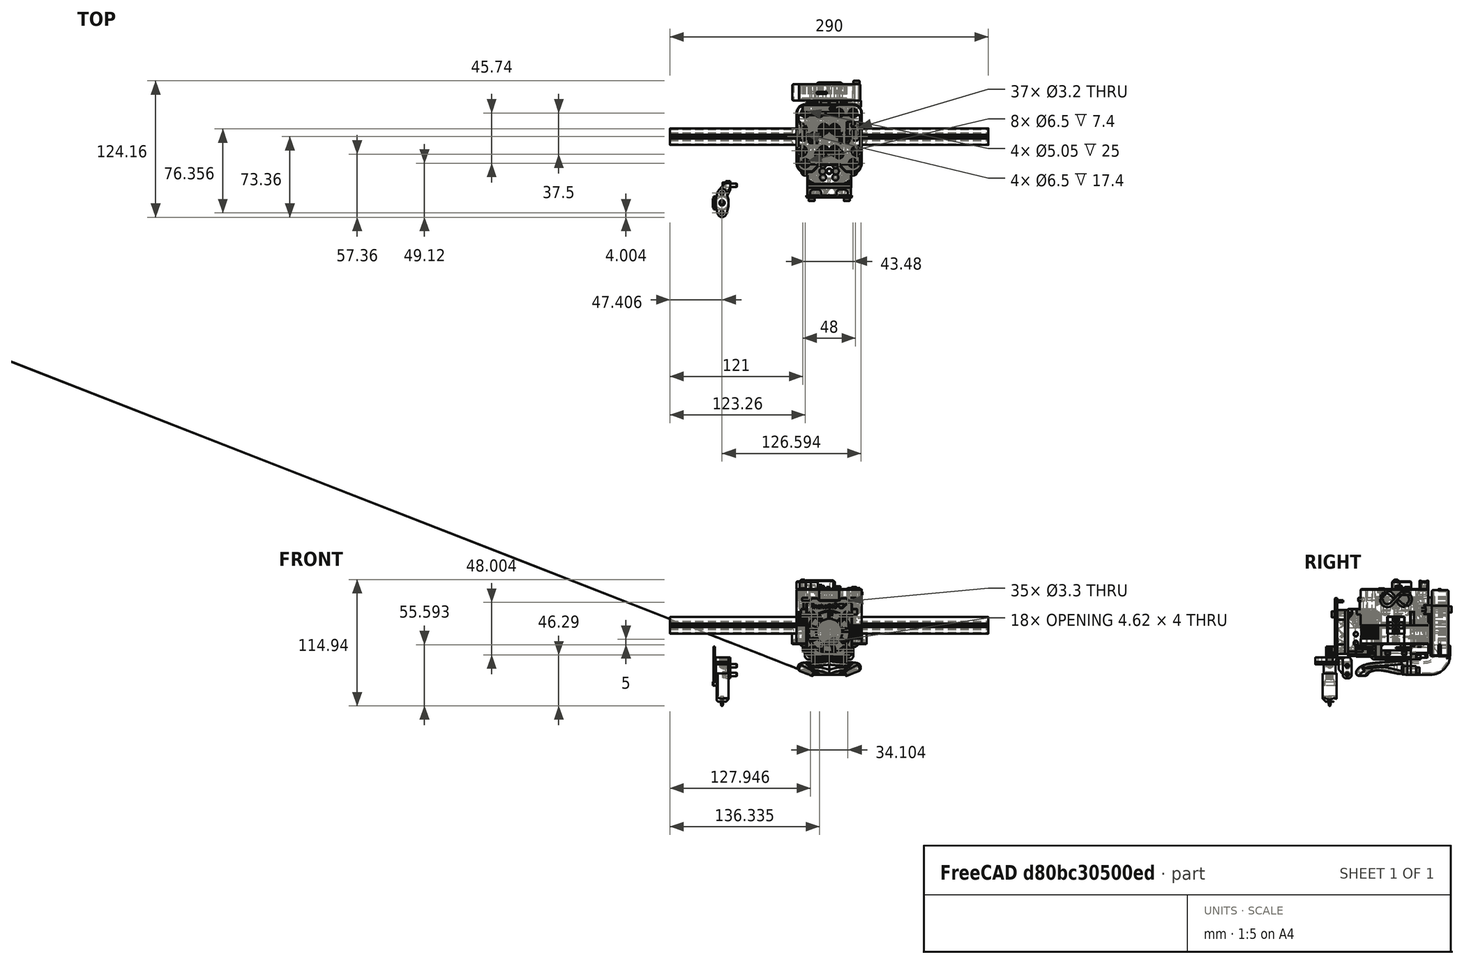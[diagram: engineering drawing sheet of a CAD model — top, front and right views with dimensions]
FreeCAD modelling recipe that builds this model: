
FCSTD DOCUMENT  (FreeCAD 0.19R24291 (Git))
Label: gantry-1515
License: Other
LicenseURL: GPL3
objects: Part::FeaturePython×95, Part::Feature×65, App::Part×6
note: 160 computed .brp shape members not serialized (recipe doc carries the construction recipe); baked Part::Feature solids carry a one-line shape summary decoded from their .brp

FEATURE [Part::FeaturePython] Screw003  label="M5x50-Screw"  # Fasteners workbench fastener (typed FeaturePython)
  Placement = pos=(9,-16,3) rot=(1,0,0;3.14159rad)
  diameter = 3
  invert = true
  length = 11
  lengthCustom = 50
  matchOuter = true
  offset = 0
  thread = false
  type = 39
FEATURE [Part::FeaturePython] Washer006  label="M3-Washer006"  # Fasteners workbench fastener (typed FeaturePython)
  Placement = pos=(-5,-13,50) rot=(0,0,1;0rad)
  diameter = 4
  invert = false
  matchOuter = true
  offset = 0
  type = 5
FEATURE [Part::FeaturePython] Screw009  label="M3x10-Screw004"  # Fasteners workbench fastener (typed FeaturePython)
  Placement = pos=(-5,-13,50.55) rot=(0,0,1;0rad)
  baseObject = -> Washer006 [Edge1]
  diameter = 4
  invert = false
  length = 3
  lengthCustom = 10
  matchOuter = true
  offset = 0
  thread = false
  type = 33
FEATURE [Part::FeaturePython] Screw005  label="M5x50-Screw005"  # Fasteners workbench fastener (typed FeaturePython)
  Placement = pos=(21.74,21.5,3) rot=(1,0,0;3.14159rad)
  diameter = 3
  invert = true
  length = 11
  lengthCustom = 50
  matchOuter = true
  offset = 0
  thread = false
  type = 39
FEATURE [Part::FeaturePython] Washer015  label="M3-Washer036"  # Fasteners workbench fastener (typed FeaturePython)
  Placement = pos=(24,0,35.55) rot=(0,0,1;0rad)
  diameter = 4
  invert = false
  matchOuter = true
  offset = 0
  type = 5
FEATURE [Part::FeaturePython] Washer011  label="M3-Washer039"  # Fasteners workbench fastener (typed FeaturePython)
  Placement = pos=(29,0,6.45) rot=(1,0,0;3.14159rad)
  diameter = 4
  invert = false
  matchOuter = true
  offset = 0
  type = 5
FEATURE [Part::FeaturePython] Screw012  label="M3x10-Screw193"  # Fasteners workbench fastener (typed FeaturePython)
  Placement = pos=(29,0,5.9) rot=(-1,0,0;3.14159rad)
  baseObject = -> Washer011 [Edge1]
  diameter = 4
  invert = false
  length = 3
  lengthCustom = 10
  matchOuter = true
  offset = 0
  thread = false
  type = 33
FEATURE [Part::FeaturePython] Washer010  label="M3-Washer038"  # Fasteners workbench fastener (typed FeaturePython)
  Placement = pos=(21,0,7.45) rot=(1,0,0;3.14159rad)
  diameter = 4
  invert = false
  matchOuter = true
  offset = 0
  type = 5
FEATURE [Part::FeaturePython] Screw011  label="M3x10-Screw192"  # Fasteners workbench fastener (typed FeaturePython)
  Placement = pos=(21,0,6.9) rot=(-1,0,0;3.14159rad)
  baseObject = -> Washer010 [Edge1]
  diameter = 4
  invert = false
  length = 3
  lengthCustom = 10
  matchOuter = true
  offset = 0
  thread = false
  type = 33
FEATURE [Part::FeaturePython] Screw004  label="M5x50-Screw004"  # Fasteners workbench fastener (typed FeaturePython)
  Placement = pos=(9,21.5,3) rot=(1,0,0;3.14159rad)
  diameter = 3
  invert = true
  length = 11
  lengthCustom = 50
  matchOuter = true
  offset = 0
  thread = false
  type = 39
FEATURE [Part::FeaturePython] Washer009  label="M3-Washer037"  # Fasteners workbench fastener (typed FeaturePython)
  Placement = pos=(13,0,6.45) rot=(1,0,0;3.14159rad)
  diameter = 4
  invert = false
  matchOuter = true
  offset = 0
  type = 5
FEATURE [Part::FeaturePython] Screw  label="M3x10-Screw191"  # Fasteners workbench fastener (typed FeaturePython)
  Placement = pos=(13,0,5.9) rot=(-1,0,0;3.14159rad)
  baseObject = -> Washer009 [Edge1]
  diameter = 4
  invert = false
  length = 3
  lengthCustom = 10
  matchOuter = true
  offset = 0
  thread = false
  type = 33
FEATURE [Part::FeaturePython] Washer004  label="M3-Washer004"  # Fasteners workbench fastener (typed FeaturePython)
  Placement = pos=(-25,7,50) rot=(0,0,1;0rad)
  diameter = 4
  invert = false
  matchOuter = true
  offset = 0
  type = 5
FEATURE [Part::FeaturePython] Screw007  label="M3x10-Screw"  # Fasteners workbench fastener (typed FeaturePython)
  Placement = pos=(-25,7,50.55) rot=(0,0,1;0rad)
  baseObject = -> Washer004 [Edge1]
  diameter = 4
  invert = false
  length = 3
  lengthCustom = 10
  matchOuter = true
  offset = 0
  thread = false
  type = 33
FEATURE [Part::FeaturePython] Washer003  label="M3-Washer"  # Fasteners workbench fastener (typed FeaturePython)
  Placement = pos=(-25,-13,50) rot=(0,0,1;0rad)
  diameter = 4
  invert = false
  matchOuter = true
  offset = 0
  type = 5
FEATURE [Part::FeaturePython] Screw008  label="M3x10-Screw005"  # Fasteners workbench fastener (typed FeaturePython)
  Placement = pos=(-25,-13,50.55) rot=(0,0,1;0rad)
  baseObject = -> Washer003 [Edge1]
  diameter = 4
  invert = false
  length = 3
  lengthCustom = 10
  matchOuter = true
  offset = 0
  thread = false
  type = 33
FEATURE [Part::Feature] Cut001002  label="smooth-idler"
  Placement = pos=(-2,0.5,0) rot=(0,0,1;0rad)
  shape: bbox 15 x 15 x 10 mm, 8 faces (baked)
FEATURE [Part::Feature] Chamfer030007001
  Placement = pos=(0,0,3) rot=(0,0,1;0rad)
  shape: bbox 31 x 61.74 x 17.85 mm, 119 faces (baked)
FEATURE [Part::Feature] Cut002001
  Placement = pos=(0,0,3) rot=(0,0,1;0rad)
  shape: bbox 58.24 x 61.74 x 35 mm, 468 faces (baked)
FEATURE [Part::FeaturePython] Washer005  label="M3-Washer005"  # Fasteners workbench fastener (typed FeaturePython)
  Placement = pos=(-5,7,50) rot=(0,0,1;0rad)
  diameter = 4
  invert = false
  matchOuter = true
  offset = 0
  type = 5
FEATURE [Part::FeaturePython] Screw010  label="M3x10-Screw006"  # Fasteners workbench fastener (typed FeaturePython)
  Placement = pos=(-5,7,50.55) rot=(0,0,1;0rad)
  baseObject = -> Washer005 [Edge1]
  diameter = 4
  invert = false
  length = 3
  lengthCustom = 10
  matchOuter = true
  offset = 0
  thread = false
  type = 33
FEATURE [Part::FeaturePython] Screw014  label="M3x12-Screw069"  # Fasteners workbench fastener (typed FeaturePython)
  Placement = pos=(24,0,36.1) rot=(0,0,1;0rad)
  baseObject = -> Washer015 [Edge1]
  diameter = 4
  invert = false
  length = 4
  lengthCustom = 12
  matchOuter = true
  offset = 0
  thread = false
  type = 33
FEATURE [Part::FeaturePython] Screw006  label="M5x50-Screw003"  # Fasteners workbench fastener (typed FeaturePython)
  Placement = pos=(21.74,-24.24,3) rot=(1,0,0;3.14159rad)
  diameter = 3
  invert = true
  length = 11
  lengthCustom = 50
  matchOuter = true
  offset = 0
  thread = false
  type = 39
FEATURE [Part::FeaturePython] Washer014  label="M3-Washer035"  # Fasteners workbench fastener (typed FeaturePython)
  Placement = pos=(14,0,35.55) rot=(0,0,1;0rad)
  diameter = 4
  invert = false
  matchOuter = true
  offset = 0
  type = 5
FEATURE [Part::FeaturePython] Screw013  label="M3x12-Screw"  # Fasteners workbench fastener (typed FeaturePython)
  Placement = pos=(14,0,36.1) rot=(0,0,1;0rad)
  baseObject = -> Washer014 [Edge1]
  diameter = 4
  invert = false
  length = 4
  lengthCustom = 12
  matchOuter = true
  offset = 0
  thread = false
  type = 33
FEATURE [Part::Feature] Cut002001001  label="20t-idler"
  Placement = pos=(0,-4.61,0) rot=(0,0,1;0rad)
  shape: bbox 15 x 15 x 10 mm, 31 faces (baked)
FEATURE [App::Part] Part  label="Y-carrier-left"
  Group = -> [Cut001002,Cut002001001,Washer003,Washer004,Washer005,Screw007,Washer006,Screw009,Screw008,Screw010,Screw006,Screw004,Screw005,Screw003,Cut002001,Chamfer030007001,Washer011,Washer009,Screw012,Screw011,Screw,Washer010,Washer014,Washer015,Screw014,Screw013]
  Origin = -> Origin
  Placement = pos=(-155,0,0) rot=(0,0,1;0rad)
FEATURE [Part::FeaturePython] Screw015  label="M5x50-Screw006"  # Fasteners workbench fastener (typed FeaturePython)
  Placement = pos=(-21.74,21.5,3) rot=(1,0,0;3.14159rad)
  diameter = 3
  invert = false
  length = 11
  lengthCustom = 50
  matchOuter = true
  offset = 0
  thread = false
  type = 39
FEATURE [Part::Feature] Part__Mirroring002001  label="20t-idler001"
  Placement = pos=(0,-4.61,0) rot=(0,0,1;0rad)
  shape: bbox 15 x 15 x 10 mm, 31 faces (baked)
FEATURE [Part::Feature] Part__Mirroring003001  label="smooth-idler001"
  Placement = pos=(2,0.5,0) rot=(0,0,1;0rad)
  shape: bbox 15 x 15 x 10 mm, 8 faces (baked)
FEATURE [Part::Feature] Chamfer010001
  Placement = pos=(0,0,3) rot=(0,0,1;0rad)
  shape: bbox 31 x 61.74 x 19 mm, 118 faces (baked)
FEATURE [Part::FeaturePython] Washer018  label="M3-Washer020"  # Fasteners workbench fastener (typed FeaturePython)
  Placement = pos=(-13,0,7) rot=(1,0,0;3.14159rad)
  baseObject = -> Chamfer010001 [Edge6]
  diameter = 4
  invert = false
  matchOuter = true
  offset = 0
  type = 5
FEATURE [Part::FeaturePython] Washer002  label="M3-Washer022"  # Fasteners workbench fastener (typed FeaturePython)
  Placement = pos=(25,7,50) rot=(0,0,1;0rad)
  diameter = 4
  invert = true
  matchOuter = true
  offset = 0
  type = 5
FEATURE [Part::FeaturePython] Screw021  label="M3x10-Screw003"  # Fasteners workbench fastener (typed FeaturePython)
  Placement = pos=(25,7,50.55) rot=(0,0,1;0rad)
  baseObject = -> Washer002 [Edge1]
  diameter = 4
  invert = false
  length = 3
  lengthCustom = 10
  matchOuter = true
  offset = 0
  thread = false
  type = 33
FEATURE [Part::FeaturePython] Washer020  label="M3-Washer023"  # Fasteners workbench fastener (typed FeaturePython)
  Placement = pos=(25,-13,50) rot=(0,0,1;0rad)
  diameter = 4
  invert = true
  matchOuter = true
  offset = 0
  type = 5
FEATURE [Part::FeaturePython] Screw022  label="M3x10-Screw015"  # Fasteners workbench fastener (typed FeaturePython)
  Placement = pos=(25,-13,50.55) rot=(0,0,1;0rad)
  baseObject = -> Washer020 [Edge1]
  diameter = 4
  invert = false
  length = 3
  lengthCustom = 10
  matchOuter = true
  offset = 0
  thread = false
  type = 33
FEATURE [Part::FeaturePython] Screw023  label="M5x50-Screw007"  # Fasteners workbench fastener (typed FeaturePython)
  Placement = pos=(-21.74,-24.24,3) rot=(1,0,0;3.14159rad)
  diameter = 3
  invert = false
  length = 11
  lengthCustom = 50
  matchOuter = true
  offset = 0
  thread = false
  type = 39
FEATURE [Part::FeaturePython] Screw024  label="M5x50-Screw008"  # Fasteners workbench fastener (typed FeaturePython)
  Placement = pos=(-9,-16,3) rot=(1,0,0;3.14159rad)
  diameter = 3
  invert = false
  length = 11
  lengthCustom = 50
  matchOuter = true
  offset = 0
  thread = false
  type = 39
FEATURE [Part::FeaturePython] Screw002  label="M5x50-Screw009"  # Fasteners workbench fastener (typed FeaturePython)
  Placement = pos=(-9,21.5,3) rot=(1,0,0;3.14159rad)
  diameter = 3
  invert = false
  length = 11
  lengthCustom = 50
  matchOuter = true
  offset = 0
  thread = false
  type = 39
FEATURE [Part::Feature] Cut001001
  Placement = pos=(0,0,3) rot=(0,0,1;0rad)
  shape: bbox 58.24 x 61.74 x 33.85 mm, 483 faces (baked)
FEATURE [Part::FeaturePython] Washer022  label="M3-Washer040"  # Fasteners workbench fastener (typed FeaturePython)
  Placement = pos=(-24,0,35.55) rot=(0,0,1;0rad)
  diameter = 4
  invert = false
  matchOuter = true
  offset = 0
  type = 5
FEATURE [Part::FeaturePython] Washer023  label="M3-Washer025"  # Fasteners workbench fastener (typed FeaturePython)
  Placement = pos=(5,7,50) rot=(0,0,1;0rad)
  diameter = 4
  invert = true
  matchOuter = true
  offset = 0
  type = 5
FEATURE [Part::FeaturePython] Screw017  label="M3x10-Screw011"  # Fasteners workbench fastener (typed FeaturePython)
  Placement = pos=(5,7,50.55) rot=(0,0,1;0rad)
  baseObject = -> Washer023 [Edge1]
  diameter = 4
  invert = false
  length = 3
  lengthCustom = 10
  matchOuter = true
  offset = 0
  thread = false
  type = 33
FEATURE [Part::FeaturePython] Washer024  label="M3-Washer042"  # Fasteners workbench fastener (typed FeaturePython)
  Placement = pos=(-29,0,6.45) rot=(1,0,0;3.14159rad)
  diameter = 4
  invert = false
  matchOuter = true
  offset = 0
  type = 5
FEATURE [Part::FeaturePython] Screw016  label="M3x10-Screw194"  # Fasteners workbench fastener (typed FeaturePython)
  Placement = pos=(-29,0,5.9) rot=(-1,0,0;3.14159rad)
  baseObject = -> Washer024 [Edge1]
  diameter = 4
  invert = false
  length = 3
  lengthCustom = 10
  matchOuter = true
  offset = 0
  thread = false
  type = 33
FEATURE [Part::FeaturePython] Washer025  label="M3-Washer027"  # Fasteners workbench fastener (typed FeaturePython)
  Placement = pos=(5,-13,50) rot=(0,0,1;0rad)
  diameter = 4
  invert = true
  matchOuter = true
  offset = 0
  type = 5
FEATURE [Part::FeaturePython] Screw019  label="M3x10-Screw013"  # Fasteners workbench fastener (typed FeaturePython)
  Placement = pos=(5,-13,50.55) rot=(0,0,1;0rad)
  baseObject = -> Washer025 [Edge1]
  diameter = 4
  invert = false
  length = 3
  lengthCustom = 10
  matchOuter = true
  offset = 0
  thread = false
  type = 33
FEATURE [Part::FeaturePython] Screw026  label="M3x12-Screw070"  # Fasteners workbench fastener (typed FeaturePython)
  Placement = pos=(-24,0,36.1) rot=(0,0,1;0rad)
  baseObject = -> Washer022 [Edge1]
  diameter = 4
  invert = false
  length = 4
  lengthCustom = 12
  matchOuter = true
  offset = 0
  thread = false
  type = 33
FEATURE [Part::FeaturePython] Washer026  label="M3-Washer041"  # Fasteners workbench fastener (typed FeaturePython)
  Placement = pos=(-14,0,35.55) rot=(0,0,1;0rad)
  diameter = 4
  invert = false
  matchOuter = true
  offset = 0
  type = 5
FEATURE [Part::FeaturePython] Screw025  label="M3x12-Screw071"  # Fasteners workbench fastener (typed FeaturePython)
  Placement = pos=(-14,0,36.1) rot=(0,0,1;0rad)
  baseObject = -> Washer026 [Edge1]
  diameter = 4
  invert = false
  length = 4
  lengthCustom = 12
  matchOuter = true
  offset = 0
  thread = false
  type = 33
FEATURE [Part::FeaturePython] Washer027  label="M3-Washer029"  # Fasteners workbench fastener (typed FeaturePython)
  Placement = pos=(-13,0,6.45) rot=(1,0,0;3.14159rad)
  baseObject = -> Washer018 [Edge1]
  diameter = 4
  invert = false
  matchOuter = true
  offset = 0
  type = 5
FEATURE [Part::FeaturePython] Screw020  label="M3x10-Screw014"  # Fasteners workbench fastener (typed FeaturePython)
  Placement = pos=(-13,0,5.9) rot=(1,0,0;3.14159rad)
  baseObject = -> Washer027 [Edge1]
  diameter = 4
  invert = false
  length = 3
  lengthCustom = 10
  matchOuter = true
  offset = 0
  thread = false
  type = 33
FEATURE [Part::FeaturePython] Washer028  label="M3-Washer043"  # Fasteners workbench fastener (typed FeaturePython)
  Placement = pos=(-21,0,7.45) rot=(1,0,0;3.14159rad)
  diameter = 4
  invert = false
  matchOuter = true
  offset = 0
  type = 5
FEATURE [Part::FeaturePython] Screw018  label="M3x10-Screw195"  # Fasteners workbench fastener (typed FeaturePython)
  Placement = pos=(-21,0,6.9) rot=(-1,0,0;3.14159rad)
  baseObject = -> Washer028 [Edge1]
  diameter = 4
  invert = false
  length = 3
  lengthCustom = 10
  matchOuter = true
  offset = 0
  thread = false
  type = 33
FEATURE [Part::Feature] Extrude001  label="1515-290mm"
  Placement = pos=(-145,0,20) rot=(0,1,0;1.5708rad)
  shape: bbox 290 x 15 x 15 mm, 71 faces (baked)
FEATURE [Part::FeaturePython] Screw1376  label="M2.5x12-Screw"  # Fasteners workbench fastener (typed FeaturePython)
  Placement = pos=(-6,-31.5,29.2) rot=(0,0,1;0rad)
  diameter = 3
  invert = false
  length = 10
  lengthCustom = 12
  matchOuter = true
  offset = 10
  thread = false
  type = 33
FEATURE [Part::FeaturePython] Screw1377  label="M2.5x12-Screw001"  # Fasteners workbench fastener (typed FeaturePython)
  Placement = pos=(6,-31.5,29.2) rot=(0,0,1;0rad)
  diameter = 3
  invert = false
  length = 10
  lengthCustom = 12
  matchOuter = true
  offset = 10
  thread = false
  type = 33
FEATURE [Part::Feature] Part__Feature023  label="adxl345 v026"
  shape: bbox 0.1911 x 0.3 x 0.1 mm, 6 faces (baked)
FEATURE [Part::Feature] Part__Feature016  label="adxl345 v019"
  shape: bbox 0.5 x 0.5 x 0.1 mm, 6 faces (baked)
FEATURE [Part::Feature] Part__Feature017  label="adxl345 v020"
  shape: bbox 0.5 x 0.5 x 0.1 mm, 6 faces (baked)
FEATURE [Part::Feature] Part__Feature112001127  label="adxl345 v017"
  shape: bbox 0.5 x 0.5 x 0.1 mm, 6 faces (baked)
FEATURE [Part::Feature] Part__Feature112001128  label="adxl345 v004"
  shape: bbox 20 x 15 x 1.27 mm, 8 faces (baked)
FEATURE [Part::Feature] Part__Feature013  label="adxl345 v016"
  shape: bbox 0.1939 x 0.3 x 0.1 mm, 6 faces (baked)
FEATURE [Part::Feature] Part__Feature112001129  label="adxl345 v3"
  shape: bbox 6 x 3 x 0.5 mm, 6 faces (baked)
FEATURE [Part::Feature] Part__Feature030  label="adxl345 v033"
  shape: bbox 0.5 x 0.5 x 0.15 mm, 6 faces (baked)
FEATURE [Part::Feature] Part__Feature112001123  label="adxl345 v012"
  shape: bbox 0.5 x 0.5 x 0.1 mm, 6 faces (baked)
FEATURE [Part::Feature] Part__Feature112001124  label="adxl345 v010"
  shape: bbox 0.5 x 0.5 x 0.1 mm, 6 faces (baked)
FEATURE [Part::Feature] Part__Feature005  label="adxl345 v008"
  shape: bbox 0.5 x 0.5 x 0.1 mm, 6 faces (baked)
FEATURE [Part::Feature] Part__Feature004  label="adxl345 v007"
  shape: bbox 0.5 x 0.5 x 0.1 mm, 6 faces (baked)
FEATURE [Part::Feature] Part__Feature112001125  label="adxl345 v006"
  shape: bbox 0.2125 x 0.3 x 0.1 mm, 6 faces (baked)
FEATURE [Part::Feature] Part__Feature112001126  label="adxl345 v005"
  shape: bbox 4 x 2 x 1 mm, 6 faces (baked)
FEATURE [Part::Feature] Part__Feature012  label="adxl345 v015"
  shape: bbox 0.2125 x 0.4 x 0.1 mm, 6 faces (baked)
FEATURE [Part::Feature] Part__Feature025  label="adxl345 v028"
  shape: bbox 0.5 x 0.5 x 0.15 mm, 6 faces (baked)
FEATURE [Part::Feature] Part__Feature026  label="adxl345 v029"
  shape: bbox 0.5 x 0.5054 x 0.15 mm, 6 faces (baked)
FEATURE [Part::Feature] Part__Feature027  label="adxl345 v030"
  shape: bbox 0.5 x 0.5 x 0.15 mm, 6 faces (baked)
FEATURE [Part::Feature] Part__Feature028  label="adxl345 v031"
  shape: bbox 0.5 x 0.5054 x 0.15 mm, 6 faces (baked)
FEATURE [Part::Feature] Part__Feature029  label="adxl345 v032"
  shape: bbox 0.5 x 0.5054 x 0.15 mm, 6 faces (baked)
FEATURE [Part::Feature] Part__Feature015  label="adxl345 v018"
  shape: bbox 0.5 x 0.5 x 0.1 mm, 6 faces (baked)
FEATURE [Part::Feature] Part__Feature112001131  label="4010 FAN001"
  Placement = pos=(-2.4e-14,-43.5,14) rot=(0,0,1;0rad)
  shape: bbox 40 x 10 x 40 mm, 104 faces (baked)
FEATURE [Part::FeaturePython] Screw1373  label="M3x20-Screw024"  # Fasteners workbench fastener (typed FeaturePython)
  Placement = pos=(16,-55.5,30) rot=(1,0,0;1.5708rad)
  baseObject = -> Part__Feature112001131 [Edge124]
  diameter = 4
  invert = false
  length = 10
  lengthCustom = 20
  matchOuter = true
  offset = 2
  thread = false
  type = 33
FEATURE [Part::FeaturePython] Screw1374  label="M3x25-Screw004"  # Fasteners workbench fastener (typed FeaturePython)
  Placement = pos=(-16,-55.5,-2) rot=(1,0,0;1.5708rad)
  baseObject = -> Part__Feature112001131 [Edge127]
  diameter = 4
  invert = false
  length = 10
  lengthCustom = 25
  matchOuter = true
  offset = 2
  thread = false
  type = 33
FEATURE [Part::FeaturePython] Screw1375  label="M3x25-Screw029"  # Fasteners workbench fastener (typed FeaturePython)
  Placement = pos=(16,-55.5,-2) rot=(1,0,0;1.5708rad)
  baseObject = -> Part__Feature112001131 [Edge121]
  diameter = 4
  invert = false
  length = 10
  lengthCustom = 25
  matchOuter = true
  offset = 2
  thread = false
  type = 33
FEATURE [Part::FeaturePython] Screw1372  label="M3x20-Screw023"  # Fasteners workbench fastener (typed FeaturePython)
  Placement = pos=(-16,-55.5,30) rot=(1,0,0;1.5708rad)
  baseObject = -> Part__Feature112001131 [Edge130]
  diameter = 4
  invert = false
  length = 10
  lengthCustom = 20
  matchOuter = true
  offset = 2
  thread = false
  type = 33
FEATURE [Part::Feature] Part__Feature112001141  label="adxl345 v011"
  shape: bbox 0.5 x 2 x 0.1 mm, 6 faces (baked)
FEATURE [Part::Feature] Part__Feature112001140  label="adxl345 v009"
  shape: bbox 0.5 x 0.4946 x 0.1 mm, 6 faces (baked)
FEATURE [Part::Feature] Part__Feature011  label="adxl345 v014"
  shape: bbox 0.5 x 0.5 x 0.1 mm, 6 faces (baked)
FEATURE [Part::Feature] Part__Feature010  label="adxl345 v013"
  shape: bbox 0.5 x 0.4946 x 0.1 mm, 6 faces (baked)
FEATURE [Part::Feature] Part__Feature018  label="adxl345 v021"
  shape: bbox 0.5 x 2 x 0.1 mm, 6 faces (baked)
FEATURE [Part::Feature] Part__Feature019  label="adxl345 v022"
  shape: bbox 0.5 x 0.4946 x 0.1 mm, 6 faces (baked)
FEATURE [Part::Feature] Part__Feature020  label="adxl345 v023"
  shape: bbox 0.5 x 0.5 x 0.1 mm, 6 faces (baked)
FEATURE [Part::Feature] Part__Feature021  label="adxl345 v024"
  shape: bbox 0.5005 x 0.4962 x 0.1 mm, 6 faces (baked)
FEATURE [Part::Feature] Part__Feature022  label="adxl345 v025"
  shape: bbox 0.1911 x 0.4 x 0.1 mm, 6 faces (baked)
FEATURE [Part::Feature] Part__Feature112001139  label="BL-touch v3.x002"
  Placement = pos=(-97.5942,-60.3565,-13.2887) rot=(0,0,1;1.5708rad)
  shape: bbox 16.53 x 26.01 x 53.81 mm, 111 faces (baked)
FEATURE [Part::FeaturePython] Nut057  label="M3-Nut026"  # Fasteners workbench fastener (typed FeaturePython)
  Placement = pos=(-17.05,15.5,41) rot=(-1,0,0;1.5708rad)
  diameter = 4
  invert = false
  matchOuter = true
  offset = 0
  thread = false
  type = 7
FEATURE [Part::FeaturePython] Screw1358  label="M3x12-Screw065"  # Fasteners workbench fastener (typed FeaturePython)
  Placement = pos=(-15,18.5,-21) rot=(-1,0,0;1.5708rad)
  diameter = 4
  invert = true
  length = 10
  lengthCustom = 12
  matchOuter = true
  offset = 0
  thread = false
  type = 33
FEATURE [Part::FeaturePython] Nut004  label="M3-Nut009"  # Fasteners workbench fastener (typed FeaturePython)
  Placement = pos=(13,15.5,-7) rot=(-1,0,0;1.5708rad)
  diameter = 4
  invert = false
  matchOuter = true
  offset = 0
  thread = false
  type = 7
FEATURE [Part::FeaturePython] Nut005  label="M3-Nut030"  # Fasteners workbench fastener (typed FeaturePython)
  Placement = pos=(-13,15.5,-7) rot=(-1,0,0;1.5708rad)
  diameter = 4
  invert = false
  matchOuter = true
  offset = 0
  thread = false
  type = 7
FEATURE [Part::FeaturePython] Screw1359  label="M3x35-Screw004"  # Fasteners workbench fastener (typed FeaturePython)
  Placement = pos=(-13.0042,-16,-6.99647) rot=(1,0,0;1.5708rad)
  diameter = 4
  invert = true
  length = 10
  lengthCustom = 35
  matchOuter = true
  offset = 0
  thread = false
  type = 33
FEATURE [Part::FeaturePython] Screw1360  label="M3x35-Screw003"  # Fasteners workbench fastener (typed FeaturePython)
  Placement = pos=(12.9958,-16,-6.99647) rot=(1,0,0;1.5708rad)
  diameter = 4
  invert = true
  length = 10
  lengthCustom = 35
  matchOuter = true
  offset = 0
  thread = false
  type = 33
FEATURE [Part::FeaturePython] Screw1361  label="M3x8-Screw129"  # Fasteners workbench fastener (typed FeaturePython)
  Placement = pos=(19,-22.5,25.5) rot=(1,0,0;1.5708rad)
  diameter = 4
  invert = false
  length = 10
  lengthCustom = 8
  matchOuter = true
  offset = 0
  thread = false
  type = 33
FEATURE [Part::FeaturePython] Screw1362  label="M3x8-Screw130"  # Fasteners workbench fastener (typed FeaturePython)
  Placement = pos=(19,-22.5,11.5) rot=(1,0,0;1.5708rad)
  diameter = 4
  invert = false
  length = 10
  lengthCustom = 8
  matchOuter = true
  offset = 0
  thread = false
  type = 33
FEATURE [Part::FeaturePython] Screw1363  label="M3x8-Screw131"  # Fasteners workbench fastener (typed FeaturePython)
  Placement = pos=(-19,-22.5,13.5) rot=(1,0,0;1.5708rad)
  diameter = 4
  invert = false
  length = 10
  lengthCustom = 8
  matchOuter = true
  offset = 0
  thread = false
  type = 33
FEATURE [Part::FeaturePython] Screw1364  label="M3x8-Screw132"  # Fasteners workbench fastener (typed FeaturePython)
  Placement = pos=(-19,-22.5,-0.5) rot=(1,0,0;1.5708rad)
  diameter = 4
  invert = false
  length = 10
  lengthCustom = 8
  matchOuter = true
  offset = 0
  thread = false
  type = 33
FEATURE [Part::FeaturePython] Screw1378  label="M3x10-Screw016"  # Fasteners workbench fastener (typed FeaturePython)
  Placement = pos=(-10.0042,-9.99647,39.1513) rot=(0,0,1;0rad)
  diameter = 4
  invert = false
  length = 10
  lengthCustom = 10
  matchOuter = true
  offset = 0
  thread = false
  type = 33
FEATURE [Part::FeaturePython] Screw1380  label="M3x12-Screw066"  # Fasteners workbench fastener (typed FeaturePython)
  Placement = pos=(-21.9,-31.5,42) rot=(0,0,1;0rad)
  diameter = 4
  invert = false
  length = 10
  lengthCustom = 12
  matchOuter = true
  offset = 7
  thread = false
  type = 33
FEATURE [Part::FeaturePython] Screw1381  label="M3x12-Screw067"  # Fasteners workbench fastener (typed FeaturePython)
  Placement = pos=(21.9,-31.5,42) rot=(0,0,1;0rad)
  diameter = 4
  invert = false
  length = 10
  lengthCustom = 12
  matchOuter = true
  offset = 7
  thread = false
  type = 33
FEATURE [Part::FeaturePython] Screw027  label="M3x25-Screw"  # Fasteners workbench fastener (typed FeaturePython)
  Placement = pos=(-10.8,-38.5,27.5) rot=(1,0,0;1.5708rad)
  diameter = 4
  invert = false
  length = 10
  lengthCustom = 25
  matchOuter = true
  offset = 0
  thread = false
  type = 33
FEATURE [Part::FeaturePython] Screw1369  label="M3x25-Screw030"  # Fasteners workbench fastener (typed FeaturePython)
  Placement = pos=(10.8,-38.5,27.5) rot=(1,0,0;1.5708rad)
  diameter = 4
  invert = false
  length = 10
  lengthCustom = 25
  matchOuter = true
  offset = 0
  thread = false
  type = 33
FEATURE [Part::FeaturePython] Nut058  label="M3-Nut027"  # Fasteners workbench fastener (typed FeaturePython)
  Placement = pos=(17.05,15.5,41) rot=(-1,0,0;1.5708rad)
  diameter = 4
  invert = false
  matchOuter = true
  offset = 0
  thread = false
  type = 7
FEATURE [Part::FeaturePython] Screw1355  label="M3x40-Screw001"  # Fasteners workbench fastener (typed FeaturePython)
  Placement = pos=(-18.5,25.5,6) rot=(0,-1,0;1.5708rad)
  diameter = 4
  invert = false
  length = 10
  lengthCustom = 40
  matchOuter = true
  offset = 0
  thread = false
  type = 33
FEATURE [Part::FeaturePython] Screw1356  label="M3x40-Screw"  # Fasteners workbench fastener (typed FeaturePython)
  Placement = pos=(18.5,25.5,19) rot=(0,1,0;1.5708rad)
  diameter = 4
  invert = false
  length = 10
  lengthCustom = 40
  matchOuter = true
  offset = 0
  thread = false
  type = 33
FEATURE [Part::FeaturePython] Screw1357  label="M3x12-Screw064"  # Fasteners workbench fastener (typed FeaturePython)
  Placement = pos=(15,18.5,-21) rot=(-1,0,0;1.5708rad)
  diameter = 4
  invert = false
  length = 10
  lengthCustom = 12
  matchOuter = true
  offset = 0
  thread = false
  type = 33
FEATURE [Part::Feature] Part__Feature112001130  label="adxl345 v034"
  shape: bbox 2 x 1 x 0.3 mm, 6 faces (baked)
FEATURE [Part::Feature] Part__Feature024  label="adxl345 v027"
  shape: bbox 0.5005 x 0.5054 x 0.15 mm, 6 faces (baked)
FEATURE [App::Part] adxl345_v3  label="adxl345"
  Group = -> [Part__Feature112001129,Part__Feature112001128,Part__Feature112001126,Part__Feature112001125,Part__Feature004,Part__Feature005,Part__Feature112001140,Part__Feature112001124,Part__Feature112001141,Part__Feature112001123,Part__Feature010,Part__Feature011,Part__Feature012,Part__Feature013,Part__Feature112001127,Part__Feature015,Part__Feature016,Part__Feature017,Part__Feature018,Part__Feature019,+12 more]
  Origin = -> Origin004
  Placement = pos=(-10,0.5,52.5) rot=(0,0,1;0rad)
FEATURE [Part::Feature] Fusion006002011004053036004001028003005014018035002010  label="mosquito-hotend001"
  Placement = pos=(0,-31.5,-28) rot=(0,0,1;0rad)
  shape: bbox 27.01 x 18.86 x 47.01 mm, 355 faces, 0 solids (baked)
FEATURE [Part::Feature] Part__Feature112001133  label="mosquito_support001"
  Placement = pos=(-2.78e-14,-21.6,27.5) rot=(0,0,1;0rad)
  shape: bbox 40 x 20.25 x 12 mm, 97 faces (baked)
FEATURE [Part::FeaturePython] Screw1382  label="M3x8-Screw128"  # Fasteners workbench fastener (typed FeaturePython)
  Placement = pos=(3e-15,-20.15,-6) rot=(1,0,0;1.5708rad)
  baseObject = -> Part__Feature112001133 [Edge213]
  diameter = 4
  invert = true
  length = 10
  lengthCustom = 8
  matchOuter = true
  offset = 0
  thread = false
  type = 33
FEATURE [Part::Feature] Part__Feature112001134  label="bottom_mgn12_short_duct001"
  Placement = pos=(0.00577366,-13.4565,-6.88873) rot=(0,0,1;0rad)
  shape: bbox 44.1 x 27 x 22.2 mm, 66 faces (baked)
FEATURE [Part::Feature] Part__Feature112001135  label="Duct v2.1 Straight001"
  Placement = pos=(15.0087,10.5436,-20.9887) rot=(0,0,1;0rad)
  shape: bbox 64.37 x 49.27 x 14.3 mm, 145 faces (baked)
FEATURE [Part::FeaturePython] Nut002  label="M3-Nut028"  # Fasteners workbench fastener (typed FeaturePython)
  Placement = pos=(-14.8942,8.54353,-20.9887) rot=(1,0,0;1.5708rad)
  baseObject = -> Part__Feature112001135 [Edge4]
  diameter = 4
  invert = false
  matchOuter = true
  offset = 0
  thread = false
  type = 7
FEATURE [Part::FeaturePython] Nut003  label="M3-Nut029"  # Fasteners workbench fastener (typed FeaturePython)
  Placement = pos=(15.1058,8.54353,-20.9887) rot=(1,0,0;1.5708rad)
  baseObject = -> Part__Feature112001135 [Edge7]
  diameter = 4
  invert = false
  matchOuter = true
  offset = 0
  thread = false
  type = 7
FEATURE [Part::Feature] Part__Feature112001136  label="5015 fan001"
  Placement = pos=(-4.23967,32.8,25.9455) rot=(0.15487,0.698575,0.698575;3.44889rad)
  shape: bbox 61.97 x 15 x 62.93 mm, 220 faces (baked)
FEATURE [Part::FeaturePython] Screw1365  label="M4x12-Screw016"  # Fasteners workbench fastener (typed FeaturePython)
  Placement = pos=(1e-15,28.5,35) rot=(-1,0,0;1.5708rad)
  diameter = 5
  invert = false
  length = 11
  lengthCustom = 12
  matchOuter = true
  offset = 10
  thread = false
  type = 33
FEATURE [Part::FeaturePython] Screw1366  label="M4x12-Screw009"  # Fasteners workbench fastener (typed FeaturePython)
  Placement = pos=(-4,28.5,42) rot=(-1,0,0;1.5708rad)
  diameter = 5
  invert = false
  length = 11
  lengthCustom = 12
  matchOuter = true
  offset = 10
  thread = false
  type = 33
FEATURE [Part::FeaturePython] Screw1367  label="M4x12-Screw017"  # Fasteners workbench fastener (typed FeaturePython)
  Placement = pos=(4,28.5,42) rot=(-1,0,0;1.5708rad)
  diameter = 5
  invert = false
  length = 11
  lengthCustom = 12
  matchOuter = true
  offset = 10
  thread = false
  type = 33
FEATURE [Part::FeaturePython] Nut006  label="M3-Nut031"  # Fasteners workbench fastener (typed FeaturePython)
  Placement = pos=(24.8758,29.75,34.3023) rot=(1,0,0;1.5708rad)
  diameter = 4
  invert = false
  matchOuter = true
  offset = 0
  thread = false
  type = 7
FEATURE [Part::FeaturePython] Screw1368  label="M3x25-Screw027"  # Fasteners workbench fastener (typed FeaturePython)
  Placement = pos=(24.8765,47.8,34.436) rot=(-1,0,0;1.5708rad)
  baseObject = -> Part__Feature112001136 [Edge8]
  diameter = 4
  invert = false
  length = 10
  lengthCustom = 25
  matchOuter = true
  offset = 0
  thread = false
  type = 33
FEATURE [Part::FeaturePython] Screw1383  label="M3x10-Screw188"  # Fasteners workbench fastener (typed FeaturePython)
  Placement = pos=(9.99577,10.0035,39.1513) rot=(0,0,1;0rad)
  diameter = 4
  invert = true
  length = 10
  lengthCustom = 10
  matchOuter = true
  offset = 0
  thread = false
  type = 33
FEATURE [Part::FeaturePython] Screw1384  label="M3x10-Screw186"  # Fasteners workbench fastener (typed FeaturePython)
  Placement = pos=(9.99577,-9.99647,39.1513) rot=(0,0,1;0rad)
  diameter = 4
  invert = true
  length = 10
  lengthCustom = 10
  matchOuter = true
  offset = 0
  thread = false
  type = 33
FEATURE [Part::FeaturePython] Screw1385  label="M3x10-Screw187"  # Fasteners workbench fastener (typed FeaturePython)
  Placement = pos=(-10.0042,10.0035,39.1513) rot=(0,0,1;0rad)
  diameter = 4
  invert = false
  length = 10
  lengthCustom = 10
  matchOuter = true
  offset = 0
  thread = false
  type = 33
FEATURE [Part::Feature] Fusion036012039011002025018010027013001002002001002001029001  label="adxl-mount-compact001"
  Placement = pos=(0,-31.5,33) rot=(0,0,1;0rad)
  shape: bbox 22 x 12.5 x 6.5 mm, 26 faces (baked)
FEATURE [Part::FeaturePython] Screw1386  label="M3x8-Screw"  # Fasteners workbench fastener (typed FeaturePython)
  Placement = pos=(0,7.5,48.5) rot=(0,0,1;0rad)
  diameter = 1
  invert = false
  length = 1
  lengthCustom = 8
  matchOuter = true
  offset = 0
  thread = false
  type = 39
FEATURE [Part::FeaturePython] Screw1387  label="M3x6-Screw"  # Fasteners workbench fastener (typed FeaturePython)
  Placement = pos=(-7.5,2.5,53) rot=(0,0,1;0rad)
  baseObject = -> Fusion036012039011002025018010027013001002002001002001029001 [Edge2]
  diameter = 4
  invert = false
  length = 1
  lengthCustom = 6
  matchOuter = true
  offset = 2.4
  thread = false
  type = 33
FEATURE [Part::FeaturePython] Screw1388  label="M3x6-Screw105"  # Fasteners workbench fastener (typed FeaturePython)
  Placement = pos=(7.5,2.5,52.6) rot=(0,0,1;0rad)
  baseObject = -> Fusion036012039011002025018010027013001002002001002001029001 [Edge47]
  diameter = 4
  invert = false
  length = 1
  lengthCustom = 6
  matchOuter = true
  offset = 2
  thread = false
  type = 33
FEATURE [Part::FeaturePython] Screw1389  label="M3x35-Screw005"  # Fasteners workbench fastener (typed FeaturePython)
  Placement = pos=(-17.0542,-16.5,41.0035) rot=(1,0,0;1.5708rad)
  diameter = 1
  invert = true
  length = 9
  lengthCustom = 35
  matchOuter = true
  offset = 0
  thread = false
  type = 39
FEATURE [Part::FeaturePython] Screw1390  label="M3x35-Screw"  # Fasteners workbench fastener (typed FeaturePython)
  Placement = pos=(17.0458,-16.5,41.0035) rot=(1,0,0;1.5708rad)
  diameter = 1
  invert = true
  length = 9
  lengthCustom = 35
  matchOuter = true
  offset = 0
  thread = false
  type = 39
FEATURE [Part::Feature] Part__Feature112001143  label="dragon_support"
  Placement = pos=(-1.3e-14,-65.5,-44.5) rot=(1,0,0;3.14159rad)
  shape: bbox 40 x 20.25 x 9.266 mm, 50 faces (baked)
FEATURE [Part::Feature] Chamfer005021077002006007019003014001
  Placement = pos=(0,-56.5,-6) rot=(0,0,1;0rad)
  shape: bbox 41.5 x 7.5 x 53.5 mm, 789 faces (baked)
FEATURE [Part::Feature] Chamfer005021077002006007019003032007001  label="mosquito-face-compact-r003"
  Placement = pos=(0,-31.5,33) rot=(0,0,1;0rad)
  shape: bbox 51.01 x 27.77 x 40.81 mm, 154 faces (baked)
FEATURE [Part::Feature] Chamfer005021077002006007019003029001  label="dragon-face-compacr-r003"
  Placement = pos=(0,-31.5,33) rot=(0,0,1;0rad)
  shape: bbox 51.01 x 26.2 x 43.01 mm, 143 faces (baked)
FEATURE [Part::Feature] Part__Feature112001138  label="bl_touch_mount001"
  Placement = pos=(-69.5942,-39.3565,-13.2887) rot=(0,0,1;0rad)
  shape: bbox 13.25 x 33 x 19 mm, 31 faces (baked)
FEATURE [Part::FeaturePython] Screw1370  label="M3x10-Screw190"  # Fasteners workbench fastener (typed FeaturePython)
  Placement = pos=(-94.0942,-44.3565,-24.7887) rot=(0,-1,0;1.5708rad)
  baseObject = -> Part__Feature112001138 [Edge2]
  diameter = 4
  invert = false
  length = 10
  lengthCustom = 10
  matchOuter = true
  offset = 0
  thread = false
  type = 33
FEATURE [Part::FeaturePython] Screw1371  label="M3x10-Screw189"  # Fasteners workbench fastener (typed FeaturePython)
  Placement = pos=(-94.0942,-44.3565,-16.7887) rot=(0,-1,0;1.5708rad)
  baseObject = -> Part__Feature112001138 [Edge1]
  diameter = 4
  invert = false
  length = 10
  lengthCustom = 10
  matchOuter = true
  offset = 0
  thread = false
  type = 33
FEATURE [App::Part] BL_Touch__1_001  label="BL-Touch <1>001"
  Group = -> [Part__Feature112001138,Part__Feature112001139,Screw1371,Screw1370]
  Origin = -> Origin206
  Placement = pos=(70,8,28.5) rot=(0,0,1;0rad)
FEATURE [Part::Feature] Chamfer008011001001  label="belt-clamp-r2"
  Placement = pos=(19,-18.5,18.5) rot=(1,0,0;1.5708rad)
  shape: bbox 10.5 x 4.5 x 20 mm, 69 faces (baked)
FEATURE [Part::Feature] Chamfer005021077002006007019003032007002  label="belt-clamp-r003"
  Placement = pos=(-19,-18.5,6.5) rot=(0,0.707107,-0.707107;3.14159rad)
  shape: bbox 10.5 x 4.5 x 20 mm, 69 faces (baked)
FEATURE [Part::FeaturePython] Washer029  label="M3-Washer031"  # Fasteners workbench fastener (typed FeaturePython)
  Placement = pos=(19,-22.5,25.5) rot=(1,0,0;1.5708rad)
  baseObject = -> Chamfer008011001001 [Edge84]
  diameter = 4
  invert = false
  matchOuter = true
  offset = 0
  type = 5
FEATURE [Part::FeaturePython] Washer001  label="M3-Washer032"  # Fasteners workbench fastener (typed FeaturePython)
  Placement = pos=(19,-22.5,11.5) rot=(1,0,0;1.5708rad)
  baseObject = -> Chamfer008011001001 [Edge85]
  diameter = 4
  invert = false
  matchOuter = true
  offset = 0
  type = 5
FEATURE [Part::FeaturePython] Washer030  label="M3-Washer033"  # Fasteners workbench fastener (typed FeaturePython)
  Placement = pos=(-19,-22.5,13.5) rot=(1,0,0;1.5708rad)
  baseObject = -> Chamfer005021077002006007019003032007002 [Edge85]
  diameter = 4
  invert = false
  matchOuter = true
  offset = 0
  type = 5
FEATURE [Part::FeaturePython] Washer031  label="M3-Washer034"  # Fasteners workbench fastener (typed FeaturePython)
  Placement = pos=(-19,-22.5,-0.5) rot=(1,0,0;1.5708rad)
  baseObject = -> Chamfer005021077002006007019003032007002 [Edge84]
  diameter = 4
  invert = false
  matchOuter = true
  offset = 0
  type = 5
FEATURE [Part::Feature] Chamfer008009001  label="belt-tesioner-block001"
  Placement = pos=(6,15,10) rot=(0,1,0;3.14159rad)
  shape: bbox 20 x 14.4 x 10 mm, 116 faces (baked)
FEATURE [Part::Feature] Chamfer005021077002006007019003032007003  label="belt-tesioner-block002"
  Placement = pos=(-6,15,15) rot=(0,0,1;0rad)
  shape: bbox 20 x 14.4 x 10 mm, 116 faces (baked)
FEATURE [Part::Feature] Chamfer008011001002001002001  label="front-plate-1515-r2"
  Placement = pos=(0,-13,10) rot=(1,0,0;1.5708rad)
  shape: bbox 48 x 8 x 57 mm, 200 faces (baked)
FEATURE [Part::Feature] Chamfer005021077002006007019003032007004  label="backplate-1515-r2"
  Placement = pos=(1e-15,10,10) rot=(0,0.707107,0.707107;3.14159rad)
  shape: bbox 50.93 x 37.34 x 72.49 mm, 492 faces (baked)
FEATURE [Part::Feature] Body001001001  label="endstop-cap-compact002"
  Placement = pos=(16,7,54) rot=(1,0,0;3.14159rad)
  shape: bbox 12 x 13 x 7.75 mm, 19 faces (baked)
FEATURE [Part::Feature] Fusion006002011004053036004001028003005014029  label="switch003"
  Placement = pos=(28,7,46) rot=(0,0,1;1.5708rad)
  shape: bbox 12.18 x 13 x 6 mm, 43 faces (baked)
FEATURE [Part::FeaturePython] Screw1391  label="M2x10-Screw"  # Fasteners workbench fastener (typed FeaturePython)
  Placement = pos=(22.75,3.75,53) rot=(0,0,1;0rad)
  baseObject = -> Body001001001 [Edge27]
  diameter = 2
  invert = false
  length = 5
  lengthCustom = 10
  matchOuter = true
  offset = 0
  thread = false
  type = 33
FEATURE [Part::FeaturePython] Screw1392  label="M2x10-Screw001"  # Fasteners workbench fastener (typed FeaturePython)
  Placement = pos=(22.75,10.25,53) rot=(0,0,1;0rad)
  baseObject = -> Body001001001 [Edge25]
  diameter = 2
  invert = false
  length = 5
  lengthCustom = 10
  matchOuter = true
  offset = 0
  thread = false
  type = 33
FEATURE [Part::Feature] Pocket006001
  Placement = pos=(0,0,0) rot=(0,0,1;3.14159rad)
  shape: bbox 50.05 x 27 x 13 mm, 100 faces (baked)
FEATURE [Part::Feature] Chamfer005021077002006007019003032018001  label="endstop-flag-r1"
  Placement = pos=(-24,0,53) rot=(0,0,1;0rad)
  shape: bbox 19.25 x 17.5 x 17 mm, 46 faces (baked)
FEATURE [Part::FeaturePython] Screw1393  label="M3x12-Screw068"  # Fasteners workbench fastener (typed FeaturePython)
  Placement = pos=(-24,0,60) rot=(0,0,1;0rad)
  baseObject = -> Chamfer005021077002006007019003032018001 [Edge47]
  diameter = 1
  invert = false
  length = 3
  lengthCustom = 12
  matchOuter = true
  offset = 0
  thread = false
  type = 39
FEATURE [App::Part] Part001  label="Y-carrier-right"
  Group = -> [Part__Mirroring002001,Part__Mirroring003001,Screw015,Screw024,Screw023,Screw002,Screw022,Screw021,Screw017,Screw019,Washer023,Washer025,Washer020,Washer002,Chamfer010001,Cut001001,Washer024,Screw016,Washer027,Screw018,Washer028,Screw020,Washer018,Washer026,Washer022,Screw026,Screw025,Chamfer005021077002006007019003032018001,Screw1393]
  Origin = -> Origin001
  Placement = pos=(155,0,0) rot=(0,0,1;0rad)
FEATURE [Part::Feature] Chamfer001004001
  Placement = pos=(0,29.5,32) rot=(1,0,0;1.5708rad)
  shape: bbox 32.54 x 11.83 x 29.43 mm, 93 faces (baked)
FEATURE [App::Part] Part197  label="toolhead-1515"
  Group = -> [Fusion006002011004053036004001028003005014018035002010,Part__Feature112001133,Part__Feature112001134,Part__Feature112001135,Part__Feature112001136,Part__Feature112001131,BL_Touch__1_001,Nut006,Nut058,Screw1357,Screw1358,Nut005,Nut004,Screw1355,Screw1356,Screw1365,Screw1367,Screw1366,Nut057,Screw1360,Screw1359,Nut003,Nut002,Screw1362,Screw1361,Screw1364,Screw1363,Screw1368,Screw1380,Screw1384,+40 more]
  Origin = -> Origin205
  Placement = pos=(0,0,7) rot=(0,0,1;0rad)
FEATURE [App::Part] Part002  label="gantry-1515"
  Group = -> [Part,Part001,Extrude001,Part197]
  Origin = -> Origin002
